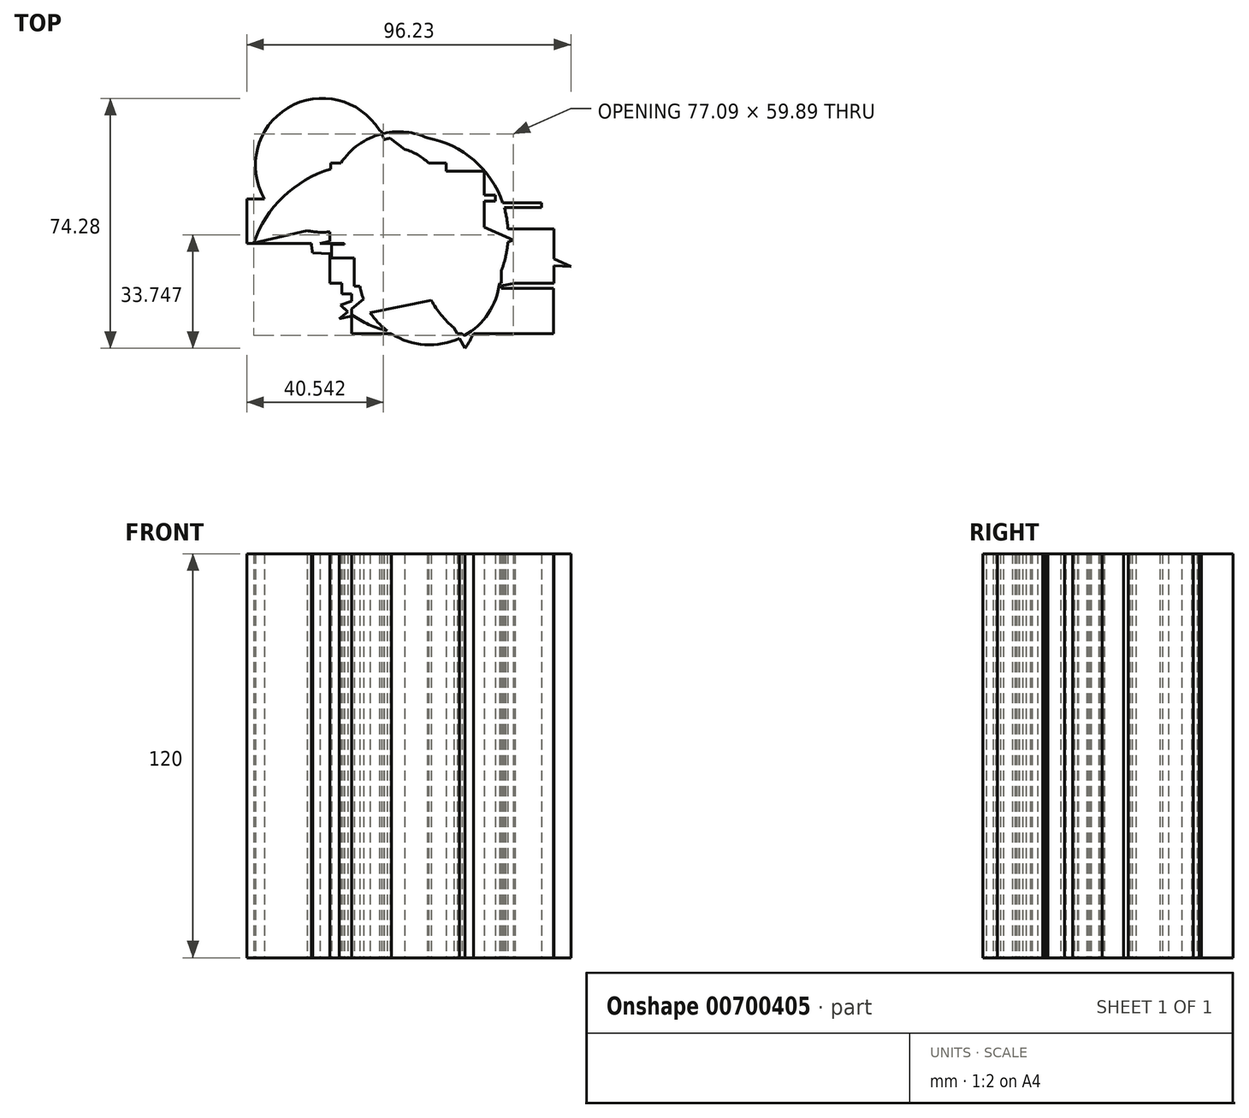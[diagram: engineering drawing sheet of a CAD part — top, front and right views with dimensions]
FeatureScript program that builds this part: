
annotation { "Feature Type Name" : "Feature", "Feature Type Description" : "" }
export const myFeature = defineFeature(function(context is Context, id is Id, definition is map)
    precondition{}
    {
        {
            var Q0;
            Q0=qCreatedBy(makeId("Top.planeOp"),FACE);
            var sketch = newSketch(context, id + "F0", { "sketchPlane" : qUnion([Q0])});
            skLineSegment(sketch, "E0", {"start": v(-35.61, 41.39) * mm, "end": v(-11.64, 10.59) * mm});
            skLineSegment(sketch, "E1", {"start": v(-16.89, 35.44) * mm, "end": v(-12.16, 7.61) * mm});
            skLineSegment(sketch, "E2", {"start": v(-44.89, 21.96) * mm, "end": v(-11.11, 14.61) * mm});
            skLineSegment(sketch, "E3", {"start": v(11.81, 17.24) * mm, "end": v(-21.79, 10.2) * mm});
            skLineSegment(sketch, "E4", {"start": v(-29.31, 13.21) * mm, "end": v(-14.17, 10.5) * mm});
            skLineSegment(sketch, "E5", {"start": v(-18.1, 16.13) * mm, "end": v(-26.16, 14.26) * mm});
            skLineSegment(sketch, "E6", {"start": v(-21.79, 20.56) * mm, "end": v(19.34, -3.59) * mm});
            skLineSegment(sketch, "E7", {"start": v(-31.59, 45.76) * mm, "end": v(-8.04, 2.75) * mm});
            skLineSegment(sketch, "E8", {"start": v(-57.49, 43.84) * mm, "end": v(20.9, 8.13) * mm});
            skLineSegment(sketch, "E9", {"start": v(24.06, -4.11) * mm, "end": v(-34.56, -16.01) * mm});
            skLineSegment(sketch, "E10", {"start": v(-43.66, 4.64) * mm, "end": v(44.01, 0) * mm});
            skLineSegment(sketch, "E11", {"start": v(19.16, 16.54) * mm, "end": v(-4.57, 8.78) * mm});
            skLineSegment(sketch, "E12", {"start": v(-33.69, 32.29) * mm, "end": v(-17.38, 14.08) * mm});
            skLineSegment(sketch, "E13", {"start": v(34.39, 13.21) * mm, "end": v(-47.34, -17.59) * mm});
            skLineSegment(sketch, "E14", {"start": v(-37.19, 14.09) * mm, "end": v(-9.66, 0.9) * mm});
            skLineSegment(sketch, "E15", {"start": v(15.49, 22.31) * mm, "end": v(-1.78, 8.28) * mm});
            skLineSegment(sketch, "E16.bottom", {"start": v(-58.19, 20.39) * mm, "end": v(-22.64, 20.39) * mm});
            skLineSegment(sketch, "E16.top", {"start": v(-58.19, 7.12) * mm, "end": v(-22.64, 7.12) * mm});
            skLineSegment(sketch, "E16.left", {"start": v(-58.19, 20.39) * mm, "end": v(-58.19, 7.12) * mm});
            skLineSegment(sketch, "E16.right", {"start": v(-22.64, 20.39) * mm, "end": v(-22.64, 7.12) * mm});
            skLineSegment(sketch, "E17.bottom", {"start": v(-21.79, 28.61) * mm, "end": v(12.36, 28.61) * mm});
            skLineSegment(sketch, "E17.top", {"start": v(-21.79, 1.67) * mm, "end": v(12.36, 1.67) * mm});
            skLineSegment(sketch, "E17.left", {"start": v(-21.79, 28.61) * mm, "end": v(-21.79, 1.67) * mm});
            skLineSegment(sketch, "E17.right", {"start": v(12.36, 28.61) * mm, "end": v(12.36, 1.67) * mm});
            skLineSegment(sketch, "E18.bottom", {"start": v(11.81, 11.11) * mm, "end": v(-26.34, 11.11) * mm});
            skLineSegment(sketch, "E18.top", {"start": v(11.81, -5.51) * mm, "end": v(-26.34, -5.51) * mm});
            skLineSegment(sketch, "E18.left", {"start": v(11.81, 11.11) * mm, "end": v(11.81, -5.51) * mm});
            skLineSegment(sketch, "E18.right", {"start": v(-26.34, 11.11) * mm, "end": v(-26.34, -5.51) * mm});
            skLineSegment(sketch, "E19.bottom", {"start": v(-30.01, 1.14) * mm, "end": v(17.41, 1.14) * mm});
            skLineSegment(sketch, "E19.top", {"start": v(-30.01, -7.79) * mm, "end": v(17.41, -7.79) * mm});
            skLineSegment(sketch, "E19.left", {"start": v(-30.01, 1.14) * mm, "end": v(-30.01, -7.79) * mm});
            skLineSegment(sketch, "E19.right", {"start": v(17.41, 1.14) * mm, "end": v(17.41, -7.79) * mm});
            skLineSegment(sketch, "E20.bottom", {"start": v(32.81, -6.21) * mm, "end": v(-27.04, -6.21) * mm});
            skLineSegment(sketch, "E20.top", {"start": v(32.81, -19.69) * mm, "end": v(-27.04, -19.69) * mm});
            skLineSegment(sketch, "E20.left", {"start": v(32.81, -6.21) * mm, "end": v(32.81, -19.69) * mm});
            skLineSegment(sketch, "E20.right", {"start": v(-27.04, -6.21) * mm, "end": v(-27.04, -19.69) * mm});
            skLineSegment(sketch, "E21.bottom", {"start": v(-24.76, 1.66) * mm, "end": v(9.19, 1.66) * mm});
            skLineSegment(sketch, "E21.top", {"start": v(-24.76, 0.44) * mm, "end": v(9.19, 0.44) * mm});
            skLineSegment(sketch, "E21.left", {"start": v(-24.76, 1.66) * mm, "end": v(-24.76, 0.44) * mm});
            skLineSegment(sketch, "E21.right", {"start": v(9.19, 1.66) * mm, "end": v(9.19, 0.44) * mm});
            skLineSegment(sketch, "E22.bottom", {"start": v(18.64, 6.91) * mm, "end": v(-32.99, 6.91) * mm});
            skLineSegment(sketch, "E22.top", {"start": v(18.64, 2.89) * mm, "end": v(-3.76, 2.89) * mm});
            skLineSegment(sketch, "E22.left", {"start": v(18.64, 6.91) * mm, "end": v(18.64, 2.89) * mm});
            skLineSegment(sketch, "E22.right", {"start": v(-32.99, 6.91) * mm, "end": v(-32.99, 2.89) * mm});
            skLineSegment(sketch, "E23.bottom", {"start": v(-28.44, 17.76) * mm, "end": v(29.31, 17.76) * mm});
            skLineSegment(sketch, "E23.top", {"start": v(-28.44, 19.16) * mm, "end": v(29.31, 19.16) * mm});
            skLineSegment(sketch, "E23.left", {"start": v(-28.44, 17.76) * mm, "end": v(-28.44, 19.16) * mm});
            skLineSegment(sketch, "E23.right", {"start": v(29.31, 17.76) * mm, "end": v(29.31, 19.16) * mm});
            skCircle(sketch, "E24", {"center": v(-35.79, 30.36) * mm, "radius": 19.9 * mm});
            skArc(sketch, "E25", {"start": v(-13.15, -0.95) * mm, "mid": v(-9.2, 39.97) * mm, "end": v(-20.49, 0.44) * mm});
            skArc(sketch, "E26", {"start": v(-6.82, 2.89) * mm, "mid": v(-2.53, -11.23) * mm, "end": v(8.28, -21.26) * mm});
            skArc(sketch, "E27", {"start": v(6.62, -24.02) * mm, "mid": v(-7.07, 27.18) * mm, "end": v(-56.2, 7.28) * mm});
            skCircle(sketch, "E28", {"center": v(-3.94, -2.01) * mm, "radius": 20.97 * mm});
            skArc(sketch, "E29", {"start": v(2.2, -16.95) * mm, "mid": v(3.66, 35.67) * mm, "end": v(-38.67, 4.37) * mm});
            skArc(sketch, "E30", {"start": v(-12.42, 2.22) * mm, "mid": v(-14.88, 35.75) * mm, "end": v(-21.79, 2.85) * mm});
            skLineSegment(sketch, "E31", {"start": v(-48.92, 19.42) * mm, "end": v(-21.79, 15.28) * mm});
            skLineSegment(sketch, "E32", {"start": v(18.81, 7.09) * mm, "end": v(5.4, 4.6) * mm});
            skLineSegment(sketch, "E33", {"start": v(-13.91, 8.31) * mm, "end": v(0.44, -16.71) * mm});
            skLineSegment(sketch, "E34", {"start": v(-24.41, -5.51) * mm, "end": v(-22.13, -4.64) * mm});
            skLineSegment(sketch, "E35", {"start": v(14.26, 10.41) * mm, "end": v(-0.06, 13) * mm});
            skLineSegment(sketch, "E36", {"start": v(-34.04, 19.16) * mm, "end": v(21.96, 6.91) * mm});
            skLineSegment(sketch, "E37", {"start": v(4.29, 23.36) * mm, "end": v(-49.96, 64.31) * mm});
            skLineSegment(sketch, "E38.bottom", {"start": v(-14.53, 21.53) * mm, "end": v(3, 21.53) * mm});
            skLineSegment(sketch, "E38.top", {"start": v(-14.53, 19.69) * mm, "end": v(3, 19.69) * mm});
            skLineSegment(sketch, "E38.left", {"start": v(-14.53, 21.53) * mm, "end": v(-14.53, 19.69) * mm});
            skLineSegment(sketch, "E38.right", {"start": v(3, 21.53) * mm, "end": v(3, 19.69) * mm});
            skLineSegment(sketch, "E39.bottom", {"start": v(-35.44, 15.84) * mm, "end": v(-0.26, 15.84) * mm});
            skLineSegment(sketch, "E39.top", {"start": v(-35.44, 14.26) * mm, "end": v(-0.26, 14.26) * mm});
            skLineSegment(sketch, "E39.left", {"start": v(-35.44, 15.84) * mm, "end": v(-35.44, 14.26) * mm});
            skLineSegment(sketch, "E39.right", {"start": v(-0.26, 15.84) * mm, "end": v(-0.26, 14.26) * mm});
            skLineSegment(sketch, "E40.bottom", {"start": v(15.66, 21.44) * mm, "end": v(-28.09, 21.44) * mm});
            skLineSegment(sketch, "E40.top", {"start": v(15.66, 19.69) * mm, "end": v(-28.09, 19.69) * mm});
            skLineSegment(sketch, "E40.left", {"start": v(15.66, 21.44) * mm, "end": v(15.66, 19.69) * mm});
            skLineSegment(sketch, "E40.right", {"start": v(-28.09, 21.44) * mm, "end": v(-28.09, 19.69) * mm});
            skLineSegment(sketch, "E41.bottom", {"start": v(-33.34, 31.06) * mm, "end": v(0.96, 31.06) * mm});
            skLineSegment(sketch, "E41.top", {"start": v(-33.34, 25.64) * mm, "end": v(0.96, 25.64) * mm});
            skLineSegment(sketch, "E41.left", {"start": v(-33.34, 31.06) * mm, "end": v(-33.34, 25.64) * mm});
            skLineSegment(sketch, "E41.right", {"start": v(0.96, 31.06) * mm, "end": v(0.96, 25.64) * mm});
            skLineSegment(sketch, "E42.bottom", {"start": v(32.99, 11.46) * mm, "end": v(-15.73, 11.46) * mm});
            skLineSegment(sketch, "E42.top", {"start": v(32.99, -4.64) * mm, "end": v(-33.51, -4.64) * mm});
            skLineSegment(sketch, "E42.left", {"start": v(32.99, 11.46) * mm, "end": v(32.99, -4.64) * mm});
            skLineSegment(sketch, "E42.right", {"start": v(-33.51, 11.46) * mm, "end": v(-33.51, -4.64) * mm});
            skLineSegment(sketch, "E43.trimOffspring", {"start": v(-22.64, 10.01) * mm, "end": v(-42.44, 5.86) * mm});
            skLineSegment(sketch, "E44.trimOffspring", {"start": v(-31.93, 12.92) * mm, "end": v(-56.26, 7.26) * mm});
            skLineSegment(sketch, "E45.trimOffspring", {"start": v(-4.55, 13.8) * mm, "end": v(-34.21, 19.16) * mm});
            skLineSegment(sketch, "E46.trimOffspring", {"start": v(-6.83, 4.18) * mm, "end": v(-30.73, -15.23) * mm});
            skLineSegment(sketch, "E47.trimOffspring", {"start": v(-6.5, 8.15) * mm, "end": v(-20.92, 3.43) * mm});
            skLineSegment(sketch, "E48.trimOffspring", {"start": v(-15.14, 11.59) * mm, "end": v(-14.17, 10.5) * mm});
            skLineSegment(sketch, "E49.trimOffspring", {"start": v(-6.33, 9.1) * mm, "end": v(17.59, 4.81) * mm});
            skLineSegment(sketch, "E50.trimOffspring", {"start": v(-12.3, 8.41) * mm, "end": v(11.46, -18.11) * mm});
            skLineSegment(sketch, "E51.trimOffspring", {"start": v(-19.54, 11.46) * mm, "end": v(-33.51, 11.46) * mm});
            skLineSegment(sketch, "E52.trimOffspring", {"start": v(-6.82, 2.89) * mm, "end": v(-32.99, 2.89) * mm});
            skLineSegment(sketch, "E53.trimOffspring", {"start": v(-3.5, 2.51) * mm, "end": v(14.79, 9.54) * mm});
            skLineSegment(sketch, "E54.trimOffspring", {"start": v(-8.8, 0.48) * mm, "end": v(25.64, -16.01) * mm});
            skLineSegment(sketch, "E55.trimOffspring", {"start": v(-8.91, 0.44) * mm, "end": v(-5.7, 1.67) * mm});
            skLineSegment(sketch, "E56.trimOffspring", {"start": v(-7.16, 1.14) * mm, "end": v(6.74, -24.24) * mm});
            skLineSegment(sketch, "E57.trimOffspring", {"start": v(-0.16, 3.56) * mm, "end": v(-3.76, 2.89) * mm});
            skArc(sketch, "E58.trimOffspring", {"start": v(11.13, 30.09) * mm, "mid": v(-1.8, 19.87) * mm, "end": v(-6.83, 4.18) * mm});
            skLineSegment(sketch, "E59.trimOffspring", {"start": v(-13.7, -1.4) * mm, "end": v(-9.3, 0.29) * mm});
            skLineSegment(sketch, "E60.trimOffspring", {"start": v(32.99, 2.62) * mm, "end": v(48.91, -4.64) * mm});
            skArc(sketch, "E61.trimOffspring", {"start": v(-30.38, -11.2) * mm, "mid": v(-23.96, -15.96) * mm, "end": v(-16.5, -18.8) * mm});
            skSolve(sketch);
        }
        {
            var Q0;
            Q0 = qSketchRegion(id + "F0", true);
            extrude(context, id + "F1", {"entities" : qUnion([Q0]), "depth" : 25 * mm, "offsetDistance" : 25 * mm});
        }
        {
            var Q0;
            Q0=makeQuery(id+"F1.opExtrude","CAP_FACE",FACE,{"disambiguationData":[OSD([sQuery(id+"F0.wireOp",EDGE,"E8"),sQuery(id+"F0.wireOp",EDGE,"E9"),sQuery(id+"F0.wireOp",EDGE,"E10"),sQuery(id+"F0.wireOp",EDGE,"E13"),sQuery(id+"F0.wireOp",EDGE,"E16.bottom"),sQuery(id+"F0.wireOp",EDGE,"E16.top"),sQuery(id+"F0.wireOp",EDGE,"E16.left"),sQuery(id+"F0.wireOp",EDGE,"E17.bottom"),sQuery(id+"F0.wireOp",EDGE,"E17.right"),sQuery(id+"F0.wireOp",EDGE,"E18.top"),sQuery(id+"F0.wireOp",EDGE,"E18.right"),sQuery(id+"F0.wireOp",EDGE,"E19.top"),sQuery(id+"F0.wireOp",EDGE,"E19.left"),sQuery(id+"F0.wireOp",EDGE,"E19.right"),sQuery(id+"F0.wireOp",EDGE,"E20.bottom"),sQuery(id+"F0.wireOp",EDGE,"E20.top"),sQuery(id+"F0.wireOp",EDGE,"E20.left"),sQuery(id+"F0.wireOp",EDGE,"E20.right"),sQuery(id+"F0.wireOp",EDGE,"E22.bottom"),sQuery(id+"F0.wireOp",EDGE,"E22.top"),sQuery(id+"F0.wireOp",EDGE,"E22.left"),sQuery(id+"F0.wireOp",EDGE,"E22.right"),sQuery(id+"F0.wireOp",EDGE,"E23.bottom"),sQuery(id+"F0.wireOp",EDGE,"E23.top"),sQuery(id+"F0.wireOp",EDGE,"E23.right"),sQuery(id+"F0.wireOp",EDGE,"E24"),sQuery(id+"F0.wireOp",EDGE,"E25"),sQuery(id+"F0.wireOp",EDGE,"E26"),sQuery(id+"F0.wireOp",EDGE,"E27"),sQuery(id+"F0.wireOp",EDGE,"E28"),sQuery(id+"F0.wireOp",EDGE,"E29"),sQuery(id+"F0.wireOp",EDGE,"E30"),sQuery(id+"F0.wireOp",EDGE,"E37"),sQuery(id+"F0.wireOp",EDGE,"E40.bottom"),sQuery(id+"F0.wireOp",EDGE,"E40.top"),sQuery(id+"F0.wireOp",EDGE,"E40.left"),sQuery(id+"F0.wireOp",EDGE,"E41.bottom"),sQuery(id+"F0.wireOp",EDGE,"E41.left"),sQuery(id+"F0.wireOp",EDGE,"E41.right"),sQuery(id+"F0.wireOp",EDGE,"E42.bottom"),sQuery(id+"F0.wireOp",EDGE,"E42.top"),sQuery(id+"F0.wireOp",EDGE,"E42.left"),sQuery(id+"F0.wireOp",EDGE,"E42.right"),sQuery(id+"F0.wireOp",EDGE,"E43.trimOffspring"),sQuery(id+"F0.wireOp",EDGE,"E44.trimOffspring"),sQuery(id+"F0.wireOp",EDGE,"E46.trimOffspring"),sQuery(id+"F0.wireOp",EDGE,"E52.trimOffspring"),sQuery(id+"F0.wireOp",EDGE,"E56.trimOffspring"),sQuery(id+"F0.wireOp",EDGE,"E60.trimOffspring"),sQuery(id+"F0.wireOp",EDGE,"E61.trimOffspring")])],"isStart":true});
            extrude(context, id + "F2", {"entities" : qUnion([Q0]), "operationType" : NewBodyOperationType.ADD, "depth" : 95 * mm, "offsetDistance" : 25 * mm});
        }
    });
